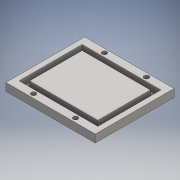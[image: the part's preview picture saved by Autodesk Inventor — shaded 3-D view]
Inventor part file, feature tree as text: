
AUTODESK INVENTOR PART (.ipt)
format: ipt  version: 2016 (Build 200138000, 138)  size: 124,416 bytes
history: native  units: mm
features: sketch x3, extrude x2, hole x1
ambient origin geometry x8: Origin, YZ Plane, XZ Plane, XY Plane, X Axis, Y Axis, Z Axis, Center Point
bodies: Solid1 (feature_tree)
feature tree (6):
  extrude  "Extrusion1"  Depth=75.0mm
  hole  "Hole1"  [1 undecoded]
  extrude  "Extrusion2"  Depth=6.0mm
  sketch  "Sketch1"  dims[d0=85.0mm d1=75.0mm]
  sketch  "Sketch2"  dims[d2=37.5mm d3=42.5mm]
  sketch  "Sketch3"  dims[d4=7.5mm d5=0.0mm d6=40.0mm d7=20.0mm d8=67.5mm d9=33.75mm d10=4.5mm d11=6.35mm d12=9.4mm d13=2.0mm d14=90.0deg d15=9.525mm d16=20.594885mm d19=75.0mm d22=60.0mm d23=30.0mm d24=5.0mm d26=37.5mm d27=5.0mm d29=5.0mm d30=5.0mm d31=6.0mm d32=0.0mm]
note: 1 required parameter value undecoded (feature->parameter linkage not recoverable at this tier; creation-order binding heuristic only, values carry confidence <= 0.55)
